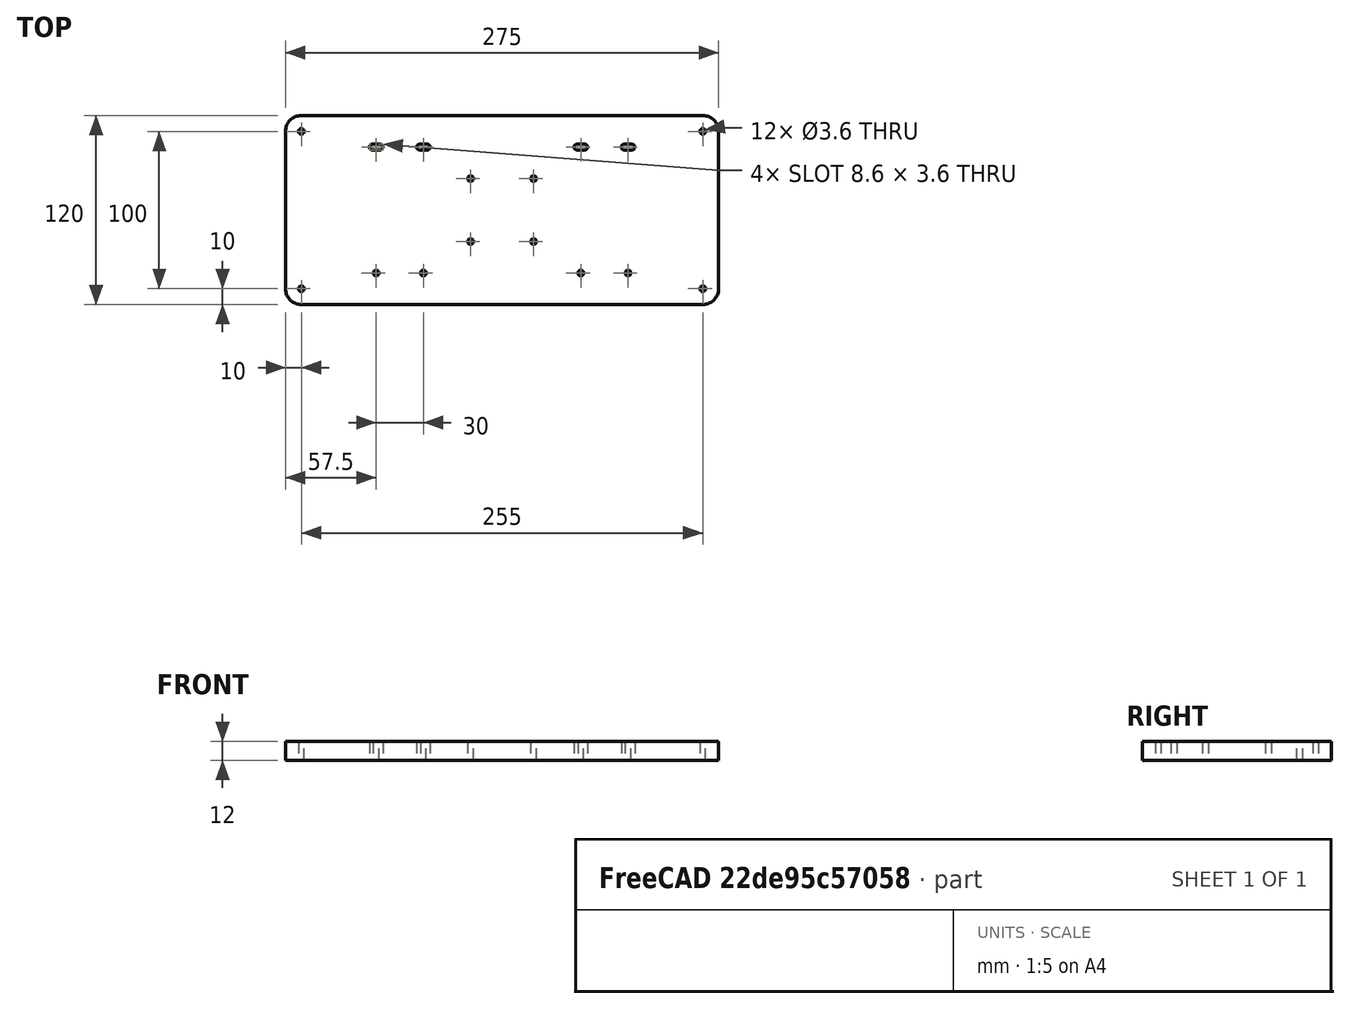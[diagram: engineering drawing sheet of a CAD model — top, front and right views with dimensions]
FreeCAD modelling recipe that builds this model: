
FCSTD DOCUMENT  (FreeCAD 0.16R6707 (Git))
Label: Y-Base
License: All rights reserved
LicenseURL: http://en.wikipedia.org/wiki/All_rights_reserved
objects: Sketcher::SketchObject×1, PartDesign::Pad×1
note: 3 computed .brp shape members not serialized (recipe doc carries the construction recipe); baked Part::Feature solids carry a one-line shape summary decoded from their .brp

FEATURE [Sketcher::SketchObject] Sketch001
  Placement = pos=(0,0,-19.5) rot=(0,0,1;0rad)
  sketch-geometry (36):
    g0: LineSegment StartX=-127.5 StartY=60 StartZ=0 EndX=127.5 EndY=60 EndZ=0
    g1: LineSegment StartX=137.5 StartY=50 StartZ=0 EndX=137.5 EndY=-50 EndZ=0
    g2: LineSegment StartX=127.5 StartY=-60 StartZ=0 EndX=-127.5 EndY=-60 EndZ=0
    g3: LineSegment StartX=-137.5 StartY=-50 StartZ=0 EndX=-137.5 EndY=50 EndZ=0
    g4: ArcOfCircle CenterX=-127.5 CenterY=50 CenterZ=0 NormalX=0 NormalY=0 NormalZ=1 Radius=10 StartAngle=1.5708 EndAngle=3.14159
    g5: ArcOfCircle CenterX=127.5 CenterY=50 CenterZ=0 NormalX=0 NormalY=0 NormalZ=1 Radius=10 StartAngle=6.28319 EndAngle=7.85398
    g6: ArcOfCircle CenterX=127.5 CenterY=-50 CenterZ=0 NormalX=0 NormalY=0 NormalZ=1 Radius=10 StartAngle=4.71239 EndAngle=6.28319
    g7: ArcOfCircle CenterX=-127.5 CenterY=-50 CenterZ=0 NormalX=0 NormalY=0 NormalZ=1 Radius=10 StartAngle=3.14159 EndAngle=4.71239
    g8: ArcOfCircle CenterX=-82.5 CenterY=40 CenterZ=0 NormalX=0 NormalY=0 NormalZ=1 Radius=1.8 StartAngle=1.5708 EndAngle=4.71239
    g9: ArcOfCircle CenterX=-77.5 CenterY=40 CenterZ=0 NormalX=0 NormalY=0 NormalZ=1 Radius=1.8 StartAngle=4.71239 EndAngle=7.85398
    g10: LineSegment StartX=-82.5 StartY=38.2 StartZ=0 EndX=-77.5 EndY=38.2 EndZ=0
    g11: LineSegment StartX=-82.5 StartY=41.8 StartZ=0 EndX=-77.5 EndY=41.8 EndZ=0
    g12: ArcOfCircle CenterX=-52.5 CenterY=40 CenterZ=0 NormalX=0 NormalY=0 NormalZ=1 Radius=1.8 StartAngle=1.5708 EndAngle=4.71239
    g13: ArcOfCircle CenterX=-47.5 CenterY=40 CenterZ=0 NormalX=0 NormalY=0 NormalZ=1 Radius=1.8 StartAngle=4.71239 EndAngle=7.85398
    g14: LineSegment StartX=-52.5 StartY=38.2 StartZ=0 EndX=-47.5 EndY=38.2 EndZ=0
    g15: LineSegment StartX=-52.5 StartY=41.8 StartZ=0 EndX=-47.5 EndY=41.8 EndZ=0
    g16: ArcOfCircle CenterX=47.5 CenterY=40 CenterZ=0 NormalX=0 NormalY=0 NormalZ=1 Radius=1.8 StartAngle=1.5708 EndAngle=4.71239
    g17: ArcOfCircle CenterX=52.5 CenterY=40 CenterZ=0 NormalX=0 NormalY=0 NormalZ=1 Radius=1.8 StartAngle=4.71239 EndAngle=7.85398
    g18: LineSegment StartX=47.5 StartY=38.2 StartZ=0 EndX=52.5 EndY=38.2 EndZ=0
    g19: LineSegment StartX=47.5 StartY=41.8 StartZ=0 EndX=52.5 EndY=41.8 EndZ=0
    g20: ArcOfCircle CenterX=77.5 CenterY=40 CenterZ=0 NormalX=0 NormalY=0 NormalZ=1 Radius=1.8 StartAngle=1.5708 EndAngle=4.71239
    g21: ArcOfCircle CenterX=82.5 CenterY=40 CenterZ=0 NormalX=0 NormalY=0 NormalZ=1 Radius=1.8 StartAngle=4.71239 EndAngle=7.85398
    g22: LineSegment StartX=77.5 StartY=38.2 StartZ=0 EndX=82.5 EndY=38.2 EndZ=0
    g23: LineSegment StartX=77.5 StartY=41.8 StartZ=0 EndX=82.5 EndY=41.8 EndZ=0
    g24: Circle CenterX=-80 CenterY=-40 CenterZ=0 NormalX=0 NormalY=0 NormalZ=1 Radius=1.8
    g25: Circle CenterX=-50 CenterY=-40 CenterZ=0 NormalX=0 NormalY=0 NormalZ=1 Radius=1.8
    g26: Circle CenterX=50 CenterY=-40 CenterZ=0 NormalX=0 NormalY=0 NormalZ=1 Radius=1.8
    g27: Circle CenterX=80 CenterY=-40 CenterZ=0 NormalX=0 NormalY=0 NormalZ=1 Radius=1.8
    g28: Circle CenterX=-127.5 CenterY=-50 CenterZ=0 NormalX=0 NormalY=0 NormalZ=1 Radius=1.8
    g29: Circle CenterX=-127.5 CenterY=50 CenterZ=0 NormalX=0 NormalY=0 NormalZ=1 Radius=1.8
    g30: Circle CenterX=127.5 CenterY=50 CenterZ=0 NormalX=0 NormalY=0 NormalZ=1 Radius=1.8
    g31: Circle CenterX=127.5 CenterY=-50 CenterZ=0 NormalX=0 NormalY=0 NormalZ=1 Radius=1.8
    g32: Circle CenterX=-20 CenterY=20 CenterZ=0 NormalX=0 NormalY=0 NormalZ=1 Radius=1.8
    g33: Circle CenterX=20 CenterY=20 CenterZ=0 NormalX=0 NormalY=0 NormalZ=1 Radius=1.8
    g34: Circle CenterX=-20 CenterY=-20 CenterZ=0 NormalX=0 NormalY=0 NormalZ=1 Radius=1.8
    g35: Circle CenterX=20 CenterY=-20 CenterZ=0 NormalX=0 NormalY=0 NormalZ=1 Radius=1.8
  constraints (95):
    c: Horizontal(g2)
    c: Vertical(g1)
    c: Vertical(g3)
    c: DistanceX(g0,g0) = 255
    c: DistanceY(g3,g3) = 100
    c: Symmetric(g0,g0,g-2)
    c: Symmetric(g2,g0,g-1)
    c: Coincident(g7,g3)
    c: Coincident(g7,g2)
    c: Coincident(g3,g4)
    c: Coincident(g4,g0)
    c: Coincident(g0,g5)
    c: Coincident(g5,g1)
    c: Coincident(g1,g6)
    c: Coincident(g6,g2)
    c: Tangent(g6,g1)
    c: Tangent(g5,g1)
    c: Tangent(g5,g0)
    c: Tangent(g2,g7)
    c: Tangent(g7,g3)
    c: Tangent(g3,g4)
    c: Tangent(g4,g0)
    c: Tangent(g6,g2)
    c: Equal(g4,g7)
    c: Equal(g7,g6)
    c: Radius(g4) = 10
    c: Tangent(g8,g11) = 1.5708
    c: Tangent(g8,g10) = -1.5708
    c: Tangent(g10,g9) = -1.5708
    c: Tangent(g11,g9) = 1.5708
    c: Horizontal(g10)
    c: Equal(g8,g9)
    c: Tangent(g12,g15) = 1.5708
    c: Tangent(g12,g14) = -1.5708
    c: Tangent(g14,g13) = -1.5708
    c: Tangent(g15,g13) = 1.5708
    c: Horizontal(g14)
    c: Equal(g12,g13)
    c: Tangent(g16,g19) = 1.5708
    c: Tangent(g16,g18) = -1.5708
    c: Tangent(g18,g17) = -1.5708
    c: Tangent(g19,g17) = 1.5708
    c: Horizontal(g18)
    c: Equal(g16,g17)
    c: Tangent(g20,g23) = 1.5708
    c: Tangent(g20,g22) = -1.5708
    c: Tangent(g22,g21) = -1.5708
    c: Tangent(g23,g21) = 1.5708
    c: Horizontal(g22)
    c: Equal(g20,g21)
    c: Radius(g24) = 1.8
    c: Equal(g24,g25)
    c: Equal(g24,g26)
    c: Equal(g24,g27)
    c: Equal(g24,g20)
    c: Equal(g24,g16)
    c: Equal(g24,g12)
    c: Equal(g24,g8)
    c: DistanceY(g25,g24) = 0
    c: DistanceY(g26,g25) = 0
    c: DistanceY(g26,g27) = 0
    c: DistanceY(g20,g17) = 0
    c: DistanceY(g16,g13) = 0
    c: DistanceY(g9,g12) = 0
    c: Symmetric(g13,g16,g-2)
    c: Symmetric(g25,g26,g-2)
    c: DistanceX(g24,g25) = 30
    c: DistanceX(g26,g27) = 30
    c: DistanceX(g25,g26) = 100
    c: DistanceX(g17,g20) = 25
    c: DistanceX(g16,g21) = 35
    c: Equal(g19,g23)
    c: Equal(g23,g15)
    c: Equal(g15,g11)
    c: DistanceX(g9,g12) = 25
    c: DistanceY(g8,g0) = 20
    c: DistanceY(g2,g24) = 20
    c: DistanceX(g13,g16) = 95
    c: Radius(g31) = 1.8
    c: Equal(g31,g30)
    c: Equal(g31,g29)
    c: Equal(g31,g28)
    c: Coincident(g28,g7)
    c: Coincident(g29,g4)
    c: Coincident(g30,g5)
    c: Coincident(g31,g6)
    c: Radius(g32) = 1.8
    c: Equal(g32,g33)
    c: Equal(g32,g34)
    c: Equal(g32,g35)
    c: Symmetric(g32,g33,g-2)
    c: Symmetric(g33,g35,g-1)
    c: Symmetric(g34,g32,g-1)
    c: DistanceX(g32,g33) = 40
    c: DistanceY(g34,g32) = 40
FEATURE [PartDesign::Pad] Pad001  label="Y-Base"
  Length = 12
  Length2 = 100
  Placement = pos=(0,0,-19.5) rot=(0,0,1;0rad)
  Sketch = -> Sketch001
  Type = 0
